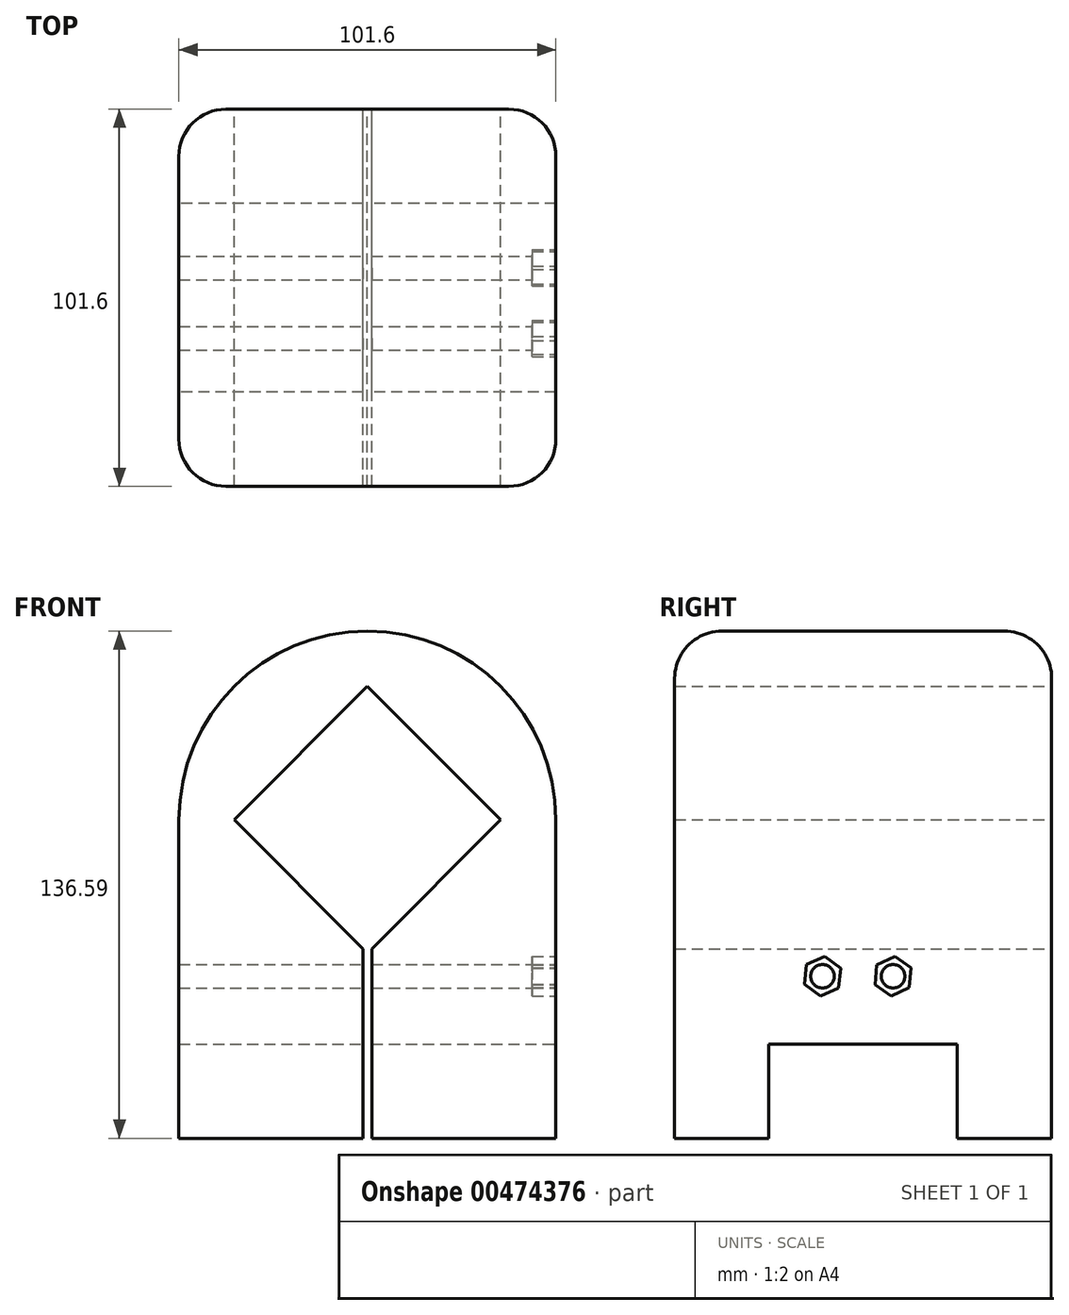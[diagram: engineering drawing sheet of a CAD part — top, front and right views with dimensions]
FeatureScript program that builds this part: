
annotation { "Feature Type Name" : "Feature", "Feature Type Description" : "" }
export const myFeature = defineFeature(function(context is Context, id is Id, definition is map)
    precondition{}
    {
        {
            var Q0;
            Q0=qCreatedBy(makeId("Front.planeOp"),FACE);
            var sketch = newSketch(context, id + "F0", { "sketchPlane" : qUnion([Q0])});
            skCircle(sketch, "E0", {"center": v(0, 0) * mm, "radius": 50.8 * mm});
            skLineSegment(sketch, "E1", {"start": v(-50.8, 0) * mm, "end": v(-50.8, -85.79) * mm});
            skLineSegment(sketch, "E2", {"start": v(-50.8, -85.79) * mm, "end": v(-50.8, -85.79) * mm});
            skLineSegment(sketch, "E3", {"start": v(50.8, 0) * mm, "end": v(50.8, -85.79) * mm});
            skLineSegment(sketch, "E4", {"start": v(50.8, -85.79) * mm, "end": v(-50.8, -85.79) * mm});
            skSolve(sketch);
        }
        {
            var Q0;
            Q0=qCreatedBy(makeId("Front.planeOp"),FACE);
            var sketch = newSketch(context, id + "F1", { "sketchPlane" : qUnion([Q0])});
            skLineSegment(sketch, "E5", {"start": v(0, 35.92) * mm, "end": v(-35.92, 0) * mm});
            skLineSegment(sketch, "E6", {"start": v(-35.92, 0) * mm, "end": v(0, -35.92) * mm});
            skLineSegment(sketch, "E7", {"start": v(0, -35.92) * mm, "end": v(35.92, 0) * mm});
            skLineSegment(sketch, "E8", {"start": v(35.92, 0) * mm, "end": v(0, 35.92) * mm});
            skSolve(sketch);
        }
        {
            var Q0;
            {var subQ0=sQuery(id+"F0.wireOp",EDGE,"E1");Q0=makeQuery(id+"F0.imprint","IMPRINT",FACE,{"disambiguationData":[TD([[makeQuery(id+"F0.imprint","IMPRINT",EDGE,{"derivedFrom":subQ0}),1.0]])]});}
            var sketch = newSketch(context, id + "F2", { "sketchPlane" : qUnion([Q0])});
            skLineSegment(sketch, "E9.bottom", {"start": v(1.18, -86.54) * mm, "end": v(-1.18, -86.54) * mm});
            skLineSegment(sketch, "E9.top", {"start": v(1.18, 14.96) * mm, "end": v(-1.18, 14.96) * mm});
            skLineSegment(sketch, "E9.left", {"start": v(1.18, -86.54) * mm, "end": v(1.18, 14.96) * mm});
            skLineSegment(sketch, "E9.right", {"start": v(-1.18, -86.54) * mm, "end": v(-1.18, 14.96) * mm});
            skPoint(sketch, "E9.middle", {"position": v(0, -35.8) * mm});
            skSolve(sketch);
        }
        {
            var Q0;
            {var subQ0=sQuery(id+"F0.wireOp",EDGE,"E1");Q0=makeQuery(id+"F0.imprint","IMPRINT",FACE,{"disambiguationData":[TD([[makeQuery(id+"F0.imprint","IMPRINT",EDGE,{"derivedFrom":subQ0}),1.0]])]});}
            var Q1;
            {var subQ0=sQuery(id+"F0.wireOp",EDGE,"E0");var subQ1=makeQuery(id+"F0.imprint","INTERSECT",VERTEX,{"derivedFrom":[subQ0,sQuery(id+"F0.wireOp",EDGE,"E1")]});Q1=makeQuery(id+"F0.imprint","IMPRINT",FACE,{"disambiguationData":[TD([[makeQuery(id+"F0.imprint","IMPRINT",EDGE,{"disambiguationData":[TD([[subQ1,1.0]])],"derivedFrom":subQ0}),1.0]])]});}
            extrude(context, id + "F3", {"entities" : qUnion([Q0, Q1]), "depth" : 101.6 * mm});
        }
        {
            var Q0;
            {var subQ0=sQuery(id+"F2.wireOp",EDGE,"E9.top");Q0=makeQuery(id+"F2.imprint","IMPRINT",FACE,{"disambiguationData":[TD([[makeQuery(id+"F2.imprint","IMPRINT",EDGE,{"derivedFrom":subQ0}),1.0]])]});}
            var Q1;
            {var subQ0=sQuery(id+"F2.wireOp",EDGE,"E9.left");var subQ1=makeQuery(id+"F0.imprint","IMPRINT",EDGE,{"derivedFrom":sQuery(id+"F0.wireOp",EDGE,"E4")});var subQ2=makeQuery(id+"F2.imprint","INTERSECT",VERTEX,{"derivedFrom":[subQ1,subQ0]});Q1=makeQuery(id+"F2.imprint","IMPRINT",FACE,{"disambiguationData":[TD([[makeQuery(id+"F2.imprint","IMPRINT",EDGE,{"disambiguationData":[TD([[subQ2,-1.0]])],"derivedFrom":subQ1}),-1.0]])]});}
            var Q2;
            Q2=makeQuery(id+"F1.imprint","IMPRINT",FACE,{"disambiguationData":[TD([[makeQuery(id+"F1.imprint","IMPRINT",EDGE,{"derivedFrom":sQuery(id+"F1.wireOp",EDGE,"E5")}),1.0]])]});
            extrude(context, id + "F4", {"entities" : qUnion([Q0, Q1, Q2]), "operationType" : NewBodyOperationType.REMOVE, "depth" : 282.66 * mm});
        }
        {
            var Q0;
            Q0=makeQuery(id+"F3.opExtrude","SWEPT_FACE",FACE,{"disambiguationData":[OSD([sQuery(id+"F0.wireOp",EDGE,"E3")])]});
            var sketch = newSketch(context, id + "F5", { "sketchPlane" : qUnion([Q0])});
            skCircle(sketch, "E10", {"center": v(-42.74, -42.16) * mm, "radius": 3.18 * mm});
            skCircle(sketch, "E11", {"center": v(-61.76, -42.16) * mm, "radius": 3.18 * mm});
            skCircle(sketch, "E12.cCircle", {"center": v(-61.76, -42.16) * mm, "radius": 5.35 * mm, "construction": true});
            skLineSegment(sketch, "E12.0", {"start": v(-57.44, -45.32) * mm, "end": v(-62.34, -47.48) * mm});
            skLineSegment(sketch, "E12.1", {"start": v(-62.34, -47.48) * mm, "end": v(-66.66, -44.32) * mm});
            skLineSegment(sketch, "E12.2", {"start": v(-66.66, -44.32) * mm, "end": v(-66.08, -39) * mm});
            skLineSegment(sketch, "E12.3", {"start": v(-66.08, -39) * mm, "end": v(-61.18, -36.84) * mm});
            skLineSegment(sketch, "E12.4", {"start": v(-61.18, -36.84) * mm, "end": v(-56.87, -40) * mm});
            skLineSegment(sketch, "E12.5", {"start": v(-56.87, -40) * mm, "end": v(-57.44, -45.32) * mm});
            skCircle(sketch, "E13.cCircle", {"center": v(-42.74, -42.16) * mm, "radius": 5.35 * mm, "construction": true});
            skLineSegment(sketch, "E13.0", {"start": v(-38.36, -45.23) * mm, "end": v(-43.2, -47.49) * mm});
            skLineSegment(sketch, "E13.1", {"start": v(-43.2, -47.49) * mm, "end": v(-47.59, -44.41) * mm});
            skLineSegment(sketch, "E13.2", {"start": v(-47.59, -44.41) * mm, "end": v(-47.12, -39.08) * mm});
            skLineSegment(sketch, "E13.3", {"start": v(-47.12, -39.08) * mm, "end": v(-42.26, -36.83) * mm});
            skLineSegment(sketch, "E13.4", {"start": v(-42.26, -36.83) * mm, "end": v(-37.88, -39.9) * mm});
            skLineSegment(sketch, "E13.5", {"start": v(-37.88, -39.9) * mm, "end": v(-38.36, -45.23) * mm});
            skSolve(sketch);
        }
        {
            var Q0;
            Q0=makeQuery(id+"F5.imprint","IMPRINT",FACE,{"disambiguationData":[TD([[makeQuery(id+"F5.imprint","IMPRINT",EDGE,{"derivedFrom":sQuery(id+"F5.wireOp",EDGE,"E10")}),1.0]])]});
            var Q1;
            Q1=makeQuery(id+"F5.imprint","IMPRINT",FACE,{"disambiguationData":[TD([[makeQuery(id+"F5.imprint","IMPRINT",EDGE,{"derivedFrom":sQuery(id+"F5.wireOp",EDGE,"E11")}),1.0]])]});
            extrude(context, id + "F6", {"entities" : qUnion([Q0, Q1]), "operationType" : NewBodyOperationType.REMOVE, "oppositeDirection" : true, "depth" : 127 * mm});
        }
        {
            var Q0;
            Q0=makeQuery(id+"F5.imprint","IMPRINT",FACE,{"disambiguationData":[TD([[makeQuery(id+"F5.imprint","IMPRINT",EDGE,{"derivedFrom":sQuery(id+"F5.wireOp",EDGE,"E11")}),-1.0]])]});
            var Q1;
            Q1=makeQuery(id+"F5.imprint","IMPRINT",FACE,{"disambiguationData":[TD([[makeQuery(id+"F5.imprint","IMPRINT",EDGE,{"derivedFrom":sQuery(id+"F5.wireOp",EDGE,"E10")}),-1.0]])]});
            extrude(context, id + "F7", {"entities" : qUnion([Q0, Q1]), "operationType" : NewBodyOperationType.REMOVE, "oppositeDirection" : true, "depth" : 6.35 * mm});
        }
        {
            var Q0;
            Q0=makeQuery(id+"F3.opExtrude","SWEPT_FACE",FACE,{"disambiguationData":[OSD([sQuery(id+"F0.wireOp",EDGE,"E3")])]});
            var sketch = newSketch(context, id + "F8", { "sketchPlane" : qUnion([Q0])});
            skLineSegment(sketch, "E14.bottom", {"start": v(-25.4, -60.39) * mm, "end": v(-76.2, -60.39) * mm});
            skLineSegment(sketch, "E14.top", {"start": v(-25.4, -111.19) * mm, "end": v(-76.2, -111.19) * mm});
            skLineSegment(sketch, "E14.left", {"start": v(-25.4, -60.39) * mm, "end": v(-25.4, -111.19) * mm});
            skLineSegment(sketch, "E14.right", {"start": v(-76.2, -60.39) * mm, "end": v(-76.2, -111.19) * mm});
            skPoint(sketch, "E14.middle", {"position": v(-50.8, -85.79) * mm});
            skSolve(sketch);
        }
        {
            var Q0;
            Q0 = qSketchRegion(id + "F8", true);
            var Q1;
            {var subQ0=sQuery(id+"F8.wireOp",EDGE,"E14.bottom");Q1=makeQuery(id+"F8.imprint","IMPRINT",FACE,{"disambiguationData":[TD([[makeQuery(id+"F8.imprint","IMPRINT",EDGE,{"derivedFrom":subQ0}),1.0]])]});}
            extrude(context, id + "F9", {"entities" : qUnion([Q0, Q1]), "operationType" : NewBodyOperationType.REMOVE, "oppositeDirection" : true, "depth" : 127 * mm});
        }
        {
            var Q0;
            Q0=makeQuery(id+"F3.opExtrude","CAP_EDGE",EDGE,{"disambiguationData":[OSD([sQuery(id+"F0.wireOp",EDGE,"E0")])],"isStart":false});
            var Q1;
            Q1=makeQuery(id+"F3.opExtrude","CAP_EDGE",EDGE,{"disambiguationData":[OSD([sQuery(id+"F0.wireOp",EDGE,"E3")])],"isStart":false});
            var Q2;
            Q2=makeQuery(id+"F3.opExtrude","CAP_EDGE",EDGE,{"disambiguationData":[OSD([sQuery(id+"F0.wireOp",EDGE,"E0")])],"isStart":true});
            var Q3;
            Q3=makeQuery(id+"F3.opExtrude","CAP_EDGE",EDGE,{"disambiguationData":[OSD([sQuery(id+"F0.wireOp",EDGE,"E3")])],"isStart":true});
            fillet(context, id + "F10", {"entities" : qUnion([Q0, Q1, Q2, Q3]), "radius" : 12.7 * mm, "tangentPropagation" : true, "allowEdgeOverflow" : false});
        }
    });
